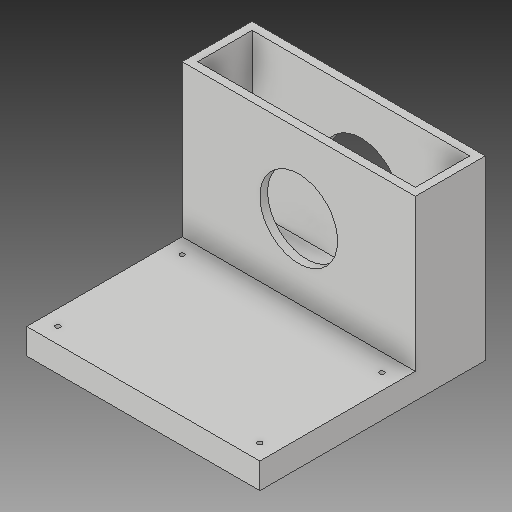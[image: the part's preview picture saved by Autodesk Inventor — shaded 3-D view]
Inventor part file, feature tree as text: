
AUTODESK INVENTOR PART (.ipt)
format: ipt  version: 2019 (Build 230136000, 136)  size: 159,232 bytes
history: native  units: mm
features: extrude x6, sketch x6
ambient origin geometry x8: Origin, YZ Plane, XZ Plane, XY Plane, X Axis, Y Axis, Z Axis, Center Point
bodies: Solid1 (feature_tree)
feature tree (12):
  extrude  "Extrusion1"  Depth=400.0mm
  extrude  "Extrusion2"  Depth=90.0mm
  extrude  "Extrusion4"  Depth=300.0mm
  extrude  "Extrusion5"  Depth=70.0mm
  extrude  "Extrusion6"  Depth=10.0mm
  extrude  "Extrusion7"  Depth=200.0mm TaperAngle=0.0deg
  sketch  "Sketch1"  dims[d0=300.0mm d1=400.0mm]
  sketch  "Sketch2"  dims[d2=90.0mm d3=0.0mm d4=100.0mm]
  sketch  "Sketch4"  dims[d5=150.0mm d6=300.0mm]
  sketch  "Sketch5"  dims[d7=100.0mm d8=0.0mm d12=70.0mm]
  sketch  "Sketch6"  dims[d13=280.0mm d14=10.0mm]
  sketch  "Sketch7"  dims[d15=10.0mm d16=200.0mm d17=0.0mm d18=195.0mm d19=33.0mm d20=200.0mm d21=0.0mm d22=172.0mm d23=0.0mm d24=20.0mm d25=20.0mm d26=6.0mm d27=20.0mm d28=20.0mm d29=20.0mm d30=20.0mm d31=20.0mm d32=20.0mm d33=50.0mm d34=0.0mm]
